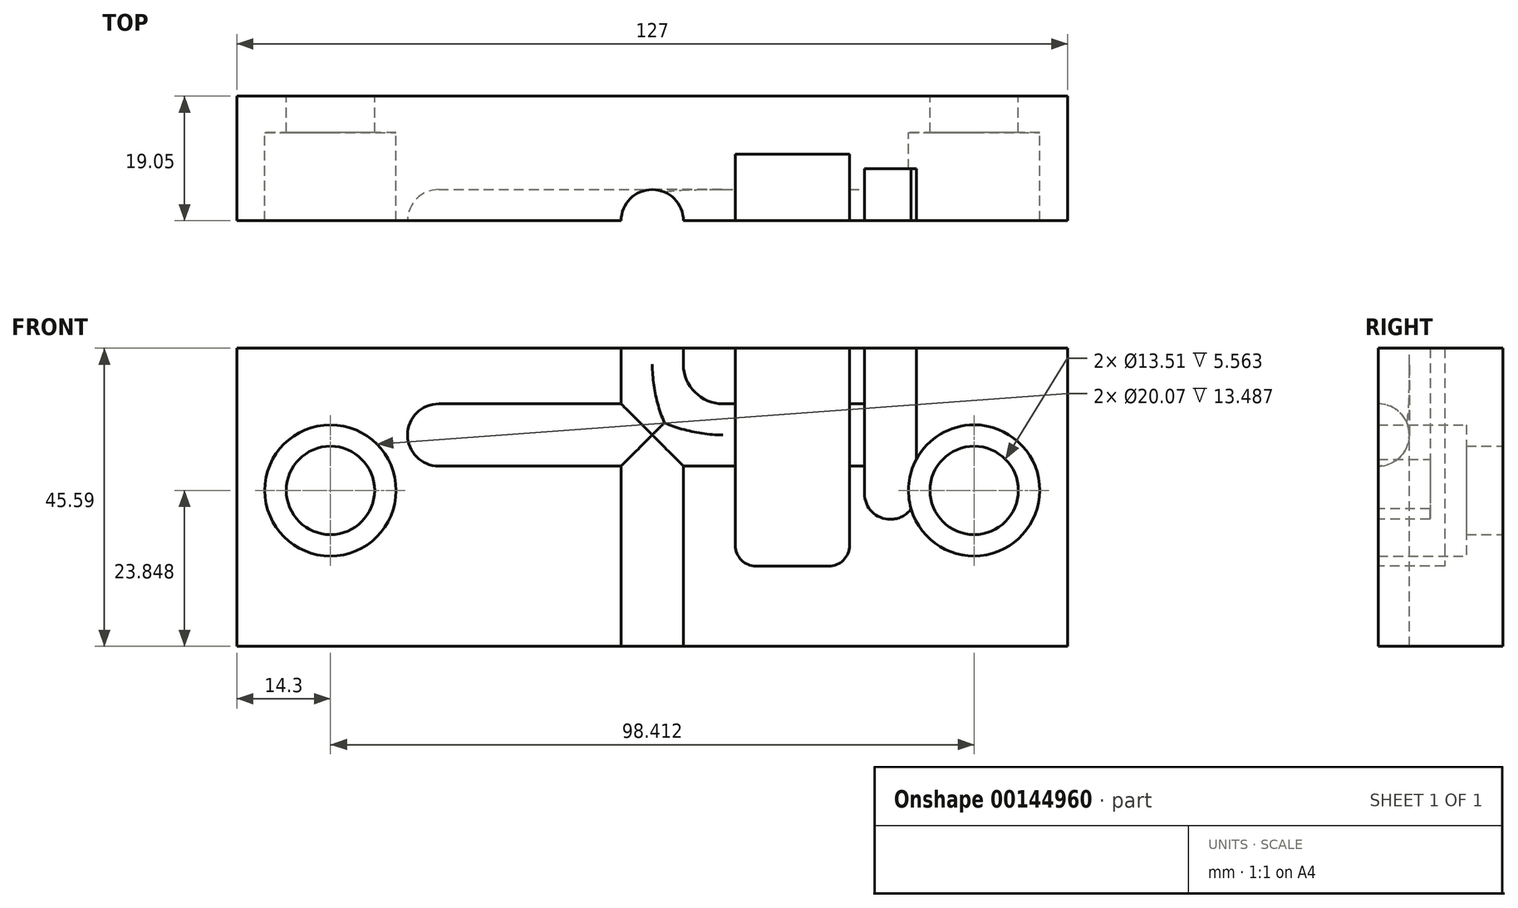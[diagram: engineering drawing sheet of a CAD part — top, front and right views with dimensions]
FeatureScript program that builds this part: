
annotation { "Feature Type Name" : "Feature", "Feature Type Description" : "" }
export const myFeature = defineFeature(function(context is Context, id is Id, definition is map)
    precondition{}
    {
        {
            var Q0;
            Q0=qCreatedBy(makeId("Front.planeOp"),FACE);
            var sketch = newSketch(context, id + "F0", { "sketchPlane" : qUnion([Q0])});
            skLineSegment(sketch, "E0", {"start": v(0, 0) * mm, "end": v(127, 0) * mm});
            skLineSegment(sketch, "E1", {"start": v(127, 0) * mm, "end": v(127, -45.6) * mm});
            skLineSegment(sketch, "E2", {"start": v(127, -45.6) * mm, "end": v(0, -45.6) * mm});
            skLineSegment(sketch, "E3", {"start": v(0, -45.6) * mm, "end": v(0, 0) * mm});
            skSolve(sketch);
        }
        {
            var Q0;
            Q0=makeQuery(id+"F0.imprint","IMPRINT",FACE,{"disambiguationData":[TD([[makeQuery(id+"F0.imprint","IMPRINT",EDGE,{"derivedFrom":sQuery(id+"F0.wireOp",EDGE,"E0")}),-1.0]])]});
            extrude(context, id + "F1", {"entities" : qUnion([Q0]), "oppositeDirection" : true, "depth" : 19.05 * mm});
        }
        {
            var Q0;
            Q0=makeQuery(id+"F1.opExtrude","CAP_FACE",FACE,{"disambiguationData":[OSD([sQuery(id+"F0.wireOp",EDGE,"E0"),sQuery(id+"F0.wireOp",EDGE,"E1"),sQuery(id+"F0.wireOp",EDGE,"E2"),sQuery(id+"F0.wireOp",EDGE,"E3")])],"isStart":true});
            var sketch = newSketch(context, id + "F2", { "sketchPlane" : qUnion([Q0])});
            skPoint(sketch, "E4", {"position": v(14.3, -21.74) * mm});
            skPoint(sketch, "E5", {"position": v(112.71, -21.74) * mm});
            skLineSegment(sketch, "E6", {"start": v(63.5, 8.43) * mm, "end": v(63.5, -53.22) * mm});
            skPoint(sketch, "E6.startSnap0", {"position": v(63.5, 0) * mm});
            skSolve(sketch);
        }
        {
            var Q0;
            Q0=sQuery(id+"F2.wireOp",VERTEX,"E4");
            var Q1;
            Q1=sQuery(id+"F2.wireOp",VERTEX,"E5");
            var Q2;
            Q2=makeQuery(id+"F1.opExtrude","SWEPT_BODY",BODY,{"disambiguationData":[OSD([sQuery(id+"F0.wireOp",EDGE,"E0"),sQuery(id+"F0.wireOp",EDGE,"E1"),sQuery(id+"F0.wireOp",EDGE,"E2"),sQuery(id+"F0.wireOp",EDGE,"E3")])]});
            hole(context, id + "F3", {"style" : HoleStyle.C_BORE, "endStyle" : HoleEndStyle.BLIND, "holeDiameter" : 13.5 * mm, "cBoreDiameter" : 20.07 * mm, "cBoreDepth" : 13.5 * mm, "holeDepth" : 19.05 * mm, "locations" : qUnion([Q0, Q1]), "scope" : qUnion([Q2]), "tappedDepth" : 12.7 * mm, "tapClearance" : 3});
        }
        {
            var Q0;
            Q0=makeQuery(id+"F1.opExtrude","SWEPT_FACE",FACE,{"disambiguationData":[OSD([sQuery(id+"F0.wireOp",EDGE,"E0")])]});
            var sketch = newSketch(context, id + "F4", { "sketchPlane" : qUnion([Q0])});
            skCircle(sketch, "E7", {"center": v(63.5, 0) * mm, "radius": 4.76 * mm});
            skSolve(sketch);
        }
        {
            var Q0;
            {var subQ0=sQuery(id+"F4.wireOp",EDGE,"E7");var subQ1=makeQuery(id+"F1.opExtrude","CAP_EDGE",EDGE,{"disambiguationData":[OSD([sQuery(id+"F0.wireOp",EDGE,"E0")])],"isStart":true});var subQ2=makeQuery(id+"F4.imprint","INTERSECT",VERTEX,{"disambiguationData":[OD(0.0)],"derivedFrom":[subQ1,subQ0]});Q0=makeQuery(id+"F4.imprint","IMPRINT",FACE,{"disambiguationData":[TD([[makeQuery(id+"F4.imprint","IMPRINT",EDGE,{"disambiguationData":[TD([[subQ2,1.0]])],"derivedFrom":subQ0}),1.0]])]});}
            var Q1;
            {var subQ0=sQuery(id+"F4.wireOp",EDGE,"E7");var subQ1=makeQuery(id+"F1.opExtrude","CAP_EDGE",EDGE,{"disambiguationData":[OSD([sQuery(id+"F0.wireOp",EDGE,"E0")])],"isStart":true});var subQ2=makeQuery(id+"F4.imprint","INTERSECT",VERTEX,{"disambiguationData":[OD(0.0)],"derivedFrom":[subQ1,subQ0]});Q1=makeQuery(id+"F4.imprint","IMPRINT",FACE,{"disambiguationData":[TD([[makeQuery(id+"F4.imprint","IMPRINT",EDGE,{"disambiguationData":[TD([[subQ2,-1.0]])],"derivedFrom":subQ0}),1.0]])]});}
            extrude(context, id + "F5", {"entities" : qUnion([Q0, Q1]), "operationType" : NewBodyOperationType.REMOVE, "oppositeDirection" : true, "depth" : 45.6 * mm});
        }
        {
            var Q0;
            {var subQ5=makeQuery(id+"F1.opExtrude","CAP_EDGE",EDGE,{"disambiguationData":[OSD([sQuery(id+"F0.wireOp",EDGE,"E1")])],"isStart":true});Q0=makeQuery(id+"F2.imprint","IMPRINT",FACE,{"disambiguationData":[TD([[makeQuery(id+"F2.imprint","IMPRINT",EDGE,{"derivedFrom":subQ5}),-1.0]])]});}
            var sketch = newSketch(context, id + "F6", { "sketchPlane" : qUnion([Q0])});
            skLineSegment(sketch, "E8", {"start": v(76.2, 0) * mm, "end": v(76.2, -30.16) * mm});
            skLineSegment(sketch, "E9", {"start": v(93.65, 0) * mm, "end": v(93.65, -30.16) * mm});
            skLineSegment(sketch, "E10", {"start": v(79.38, -33.34) * mm, "end": v(90.47, -33.34) * mm});
            skLineSegment(sketch, "E11", {"start": v(76.2, 0) * mm, "end": v(93.65, 0) * mm});
            skPoint(sketch, "E12.visualSharp", {"position": v(76.2, -33.34) * mm});
            skArc(sketch, "E12.filletArc", {"start": v(76.2, -30.16) * mm, "mid": v(77.13, -32.4) * mm, "end": v(79.38, -33.34) * mm});
            skPoint(sketch, "E13.visualSharp", {"position": v(93.65, -33.34) * mm});
            skArc(sketch, "E13.filletArc", {"start": v(90.47, -33.34) * mm, "mid": v(92.72, -32.4) * mm, "end": v(93.65, -30.16) * mm});
            skSolve(sketch);
        }
        {
            var Q0;
            Q0 = qSketchRegion(id + "F6", true);
            extrude(context, id + "F7", {"entities" : qUnion([Q0]), "operationType" : NewBodyOperationType.REMOVE, "oppositeDirection" : true, "depth" : 10.2 * mm});
        }
        {
            var Q0;
            Q0=qCreatedBy(makeId("Front.planeOp"),FACE);
            var sketch = newSketch(context, id + "F8", { "sketchPlane" : qUnion([Q0])});
            skLineSegment(sketch, "E14", {"start": v(95.94, 0) * mm, "end": v(95.94, -22.2) * mm});
            skLineSegment(sketch, "E15", {"start": v(103.87, 0) * mm, "end": v(103.87, -22.2) * mm});
            skLineSegment(sketch, "E16", {"start": v(95.94, 0) * mm, "end": v(103.87, 0) * mm});
            skLineSegment(sketch, "E17", {"start": v(99.91, -26.16) * mm, "end": v(99.9, -26.16) * mm});
            skPoint(sketch, "E18.visualSharp", {"position": v(95.94, -26.16) * mm});
            skArc(sketch, "E18.filletArc", {"start": v(95.94, -22.2) * mm, "mid": v(97.1, -25) * mm, "end": v(99.9, -26.16) * mm});
            skPoint(sketch, "E19.visualSharp", {"position": v(103.87, -26.16) * mm});
            skArc(sketch, "E19.filletArc", {"start": v(99.91, -26.16) * mm, "mid": v(102.71, -25) * mm, "end": v(103.87, -22.2) * mm});
            skSolve(sketch);
        }
        {
            var Q0;
            Q0 = qSketchRegion(id + "F8", true);
            extrude(context, id + "F9", {"entities" : qUnion([Q0]), "operationType" : NewBodyOperationType.REMOVE, "oppositeDirection" : true, "depth" : 7.94 * mm});
        }
        {
            var Q0;
            Q0=makeQuery(id+"F9.boolean.opBoolean","COPY",FACE,{"derivedFrom":makeQuery(id+"F9.opExtrude","SWEPT_FACE",FACE,{"disambiguationData":[OSD([sQuery(id+"F8.wireOp",EDGE,"E14")])]})});
            var sketch = newSketch(context, id + "F10", { "sketchPlane" : qUnion([Q0])});
            skCircle(sketch, "E20", {"center": v(0, -13.26) * mm, "radius": 4.76 * mm});
            skSolve(sketch);
        }
        {
            var Q0;
            Q0 = qSketchRegion(id + "F10", true);
            extrude(context, id + "F11", {"entities" : qUnion([Q0]), "operationType" : NewBodyOperationType.REMOVE, "oppositeDirection" : true, "depth" : 69.85 * mm});
        }
        {
            var Q0;
            Q0=makeQuery(id+"F11.boolean.opBoolean","COPY",EDGE,{"derivedFrom":makeQuery(id+"F11.opExtrude","CAP_EDGE",EDGE,{"disambiguationData":[OSD([sQuery(id+"F10.wireOp",EDGE,"E20")])],"isStart":false})});
            fillet(context, id + "F12", {"entities" : qUnion([Q0]), "radius" : 4.76 * mm, "tangentPropagation" : true, "allowEdgeOverflow" : false});
        }
        {
            var Q0;
            Q0=qCreatedBy(makeId("Front.planeOp"),FACE);
            var sketch = newSketch(context, id + "F13", { "sketchPlane" : qUnion([Q0])});
            skLineSegment(sketch, "E21", {"start": v(63.5, 0) * mm, "end": v(63.5, -2.46) * mm});
            skLineSegment(sketch, "E22", {"start": v(74.3, -13.26) * mm, "end": v(77.7, -13.26) * mm});
            skPoint(sketch, "E23.visualSharp", {"position": v(63.5, -13.26) * mm});
            skArc(sketch, "E23.filletArc", {"start": v(63.5, -2.46) * mm, "mid": v(66.66, -10.1) * mm, "end": v(74.3, -13.26) * mm});
            skSolve(sketch);
        }
        {
            var Q0;
            Q0 = qSketchRegion(id + "F4", true);
            var Q1;
            Q1=sQuery(id+"F13.wireOp",EDGE,"E23.filletArc");
            var Q2;
            Q2=sQuery(id+"F13.wireOp",EDGE,"E22");
            var Q3;
            Q3=sQuery(id+"F13.wireOp",EDGE,"E21");
            sweep(context, id + "F14", {"operationType" : NewBodyOperationType.REMOVE, "profiles" : qUnion([Q0]), "path" : qUnion([Q1, Q2, Q3])});
        }
    });
